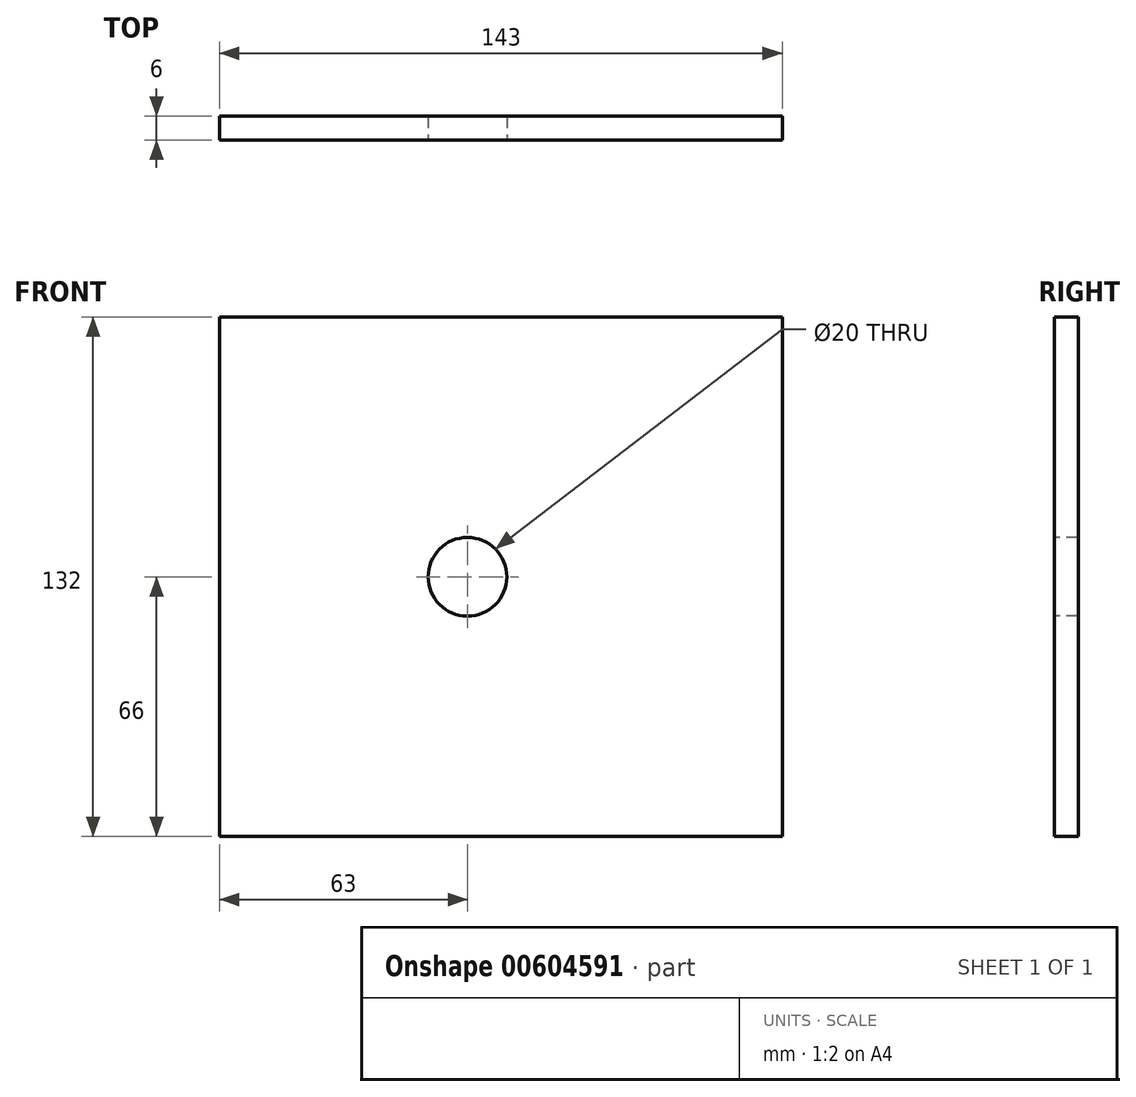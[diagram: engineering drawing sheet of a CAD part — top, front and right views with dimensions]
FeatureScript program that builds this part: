
annotation { "Feature Type Name" : "Feature", "Feature Type Description" : "" }
export const myFeature = defineFeature(function(context is Context, id is Id, definition is map)
    precondition{}
    {
        {
            var Q0;
            Q0=qCreatedBy(makeId("Front.planeOp"),FACE);
            var sketch = newSketch(context, id + "F0", { "sketchPlane" : qUnion([Q0])});
            skLineSegment(sketch, "E0", {"start": v(0, 66) * mm, "end": v(-63, 66) * mm});
            skLineSegment(sketch, "E1", {"start": v(-63, 66) * mm, "end": v(-63, -66) * mm});
            skLineSegment(sketch, "E2", {"start": v(-63, -66) * mm, "end": v(0, -66) * mm});
            skLineSegment(sketch, "E3", {"start": v(0, -66) * mm, "end": v(80, -66) * mm});
            skLineSegment(sketch, "E4", {"start": v(80, -66) * mm, "end": v(80, 66) * mm});
            skLineSegment(sketch, "E5", {"start": v(80, 66) * mm, "end": v(0, 66) * mm});
            skSolve(sketch);
        }
        {
            var Q0;
            Q0 = qSketchRegion(id + "F0", true);
            extrude(context, id + "F1", {"entities" : qUnion([Q0]), "depth" : 6 * mm, "offsetDistance" : 25 * mm});
        }
        {
            var Q0;
            Q0=makeQuery(id+"F1.opExtrude","CAP_FACE",FACE,{"disambiguationData":[OSD([sQuery(id+"F0.wireOp",EDGE,"E0"),sQuery(id+"F0.wireOp",EDGE,"E1"),sQuery(id+"F0.wireOp",EDGE,"E2"),sQuery(id+"F0.wireOp",EDGE,"E3"),sQuery(id+"F0.wireOp",EDGE,"E4"),sQuery(id+"F0.wireOp",EDGE,"E5")])],"isStart":false});
            var sketch = newSketch(context, id + "F2", { "sketchPlane" : qUnion([Q0])});
            skCircle(sketch, "E6", {"center": v(0, 0) * mm, "radius": 10 * mm});
            skSolve(sketch);
        }
        {
            var Q0;
            Q0 = qSketchRegion(id + "F2", true);
            extrude(context, id + "F3", {"entities" : qUnion([Q0]), "operationType" : NewBodyOperationType.REMOVE, "endBound" : BoundingType.THROUGH_ALL, "oppositeDirection" : true, "depth" : 25 * mm, "offsetDistance" : 25 * mm});
        }
    });
